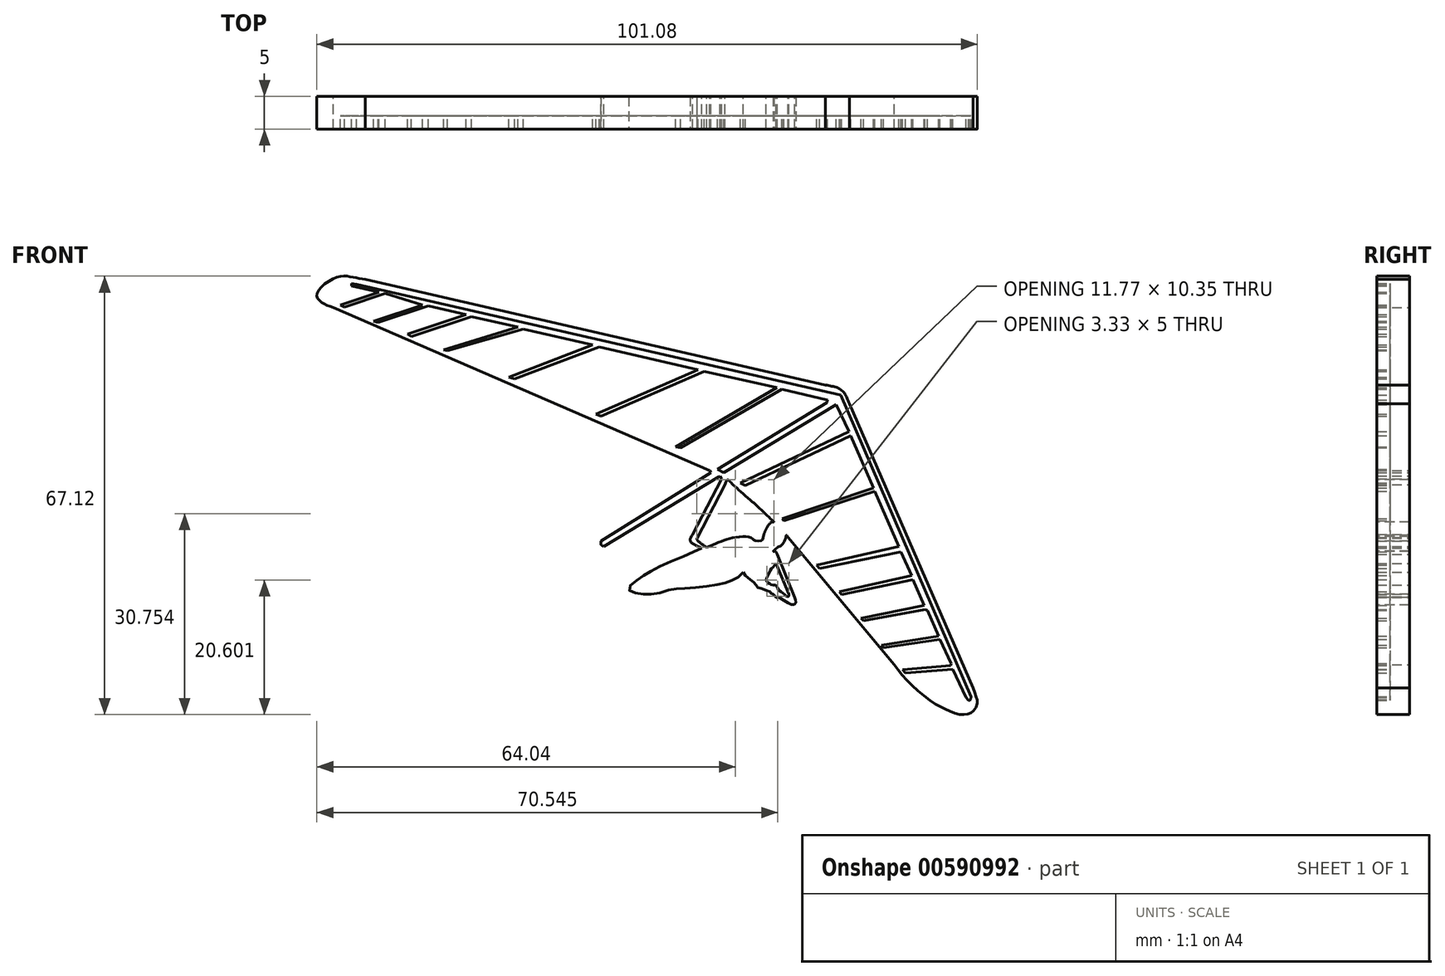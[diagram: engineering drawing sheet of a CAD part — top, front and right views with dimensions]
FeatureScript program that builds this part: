
annotation { "Feature Type Name" : "Feature", "Feature Type Description" : "" }
export const myFeature = defineFeature(function(context is Context, id is Id, definition is map)
    precondition{}
    {
        {
            var Q0;
            Q0=qCreatedBy(makeId("Front.planeOp"),FACE);
            var sketch = newSketch(context, id + "F0", { "sketchPlane" : qUnion([Q0])});
            skFitSpline(sketch, "E0", {"points": [v(-69.22, 30.45) * mm, v(-71.12, 31.32) * mm, v(-71.66, 32.62) * mm, v(-68.68, 35.07) * mm, v(-66.35, 35.12) * mm, v(-64.29, 34.74) * mm], "startDerivative": vector(-10.93, 3.69) * mm, "endDerivative": vector(10.85, -2) * mm});
            skFitSpline(sketch, "E1", {"points": [v(6.12, 18.58) * mm, v(8, 18.14) * mm, v(9.02, 17.32) * mm, v(9.77, 15.73) * mm], "startDerivative": vector(5.63, -0.88) * mm, "endDerivative": vector(1.94, -5.07) * mm});
            skLineSegment(sketch, "E2", {"start": v(-64.29, 34.74) * mm, "end": v(6.12, 18.58) * mm});
            skLineSegment(sketch, "E3", {"start": v(9.77, 15.73) * mm, "end": v(28.73, -27.8) * mm});
            skFitSpline(sketch, "E4", {"points": [v(28.73, -27.8) * mm, v(29.23, -29.25) * mm, v(29.34, -30.21) * mm, v(28.73, -31.36) * mm, v(28, -31.75) * mm, v(26.66, -31.82) * mm, v(24.7, -31.13) * mm, v(22.51, -29.98) * mm, v(18.95, -26.99) * mm, v(16.65, -24.23) * mm], "startDerivative": vector(5.52, -15.59) * mm, "endDerivative": vector(-13.52, 17.82) * mm});
            skLineSegment(sketch, "E5", {"start": v(16.65, -24.23) * mm, "end": v(0.4, -4.7) * mm});
            skFitSpline(sketch, "E6", {"points": [v(0.4, -4.7) * mm, v(0.16, -4.41) * mm, v(0, -4.91) * mm, v(-0.32, -5.6) * mm, v(-0.74, -6.05) * mm, v(-1.2, -6.27) * mm, v(-1.74, -6.74) * mm, v(-1.86, -6.88) * mm, v(-1.59, -6.85) * mm, v(-1.25, -7.34) * mm], "startDerivative": vector(-2.75, 4.77) * mm, "endDerivative": vector(2.1, -5.53) * mm});
            skLineSegment(sketch, "E7", {"start": v(-1.25, -7.34) * mm, "end": v(1.41, -13.93) * mm});
            skFitSpline(sketch, "E8", {"points": [v(1.41, -13.93) * mm, v(1.57, -14.39) * mm, v(1.54, -14.85) * mm, v(1.18, -15.06) * mm, v(0.45, -14.76) * mm, v(-0.65, -14.13) * mm, v(-1.02, -13.93) * mm, v(-1.45, -13.93) * mm, v(-1.58, -13.74) * mm, v(-1.86, -13.45) * mm, v(-2.2, -13.35) * mm, v(-2.28, -13.1) * mm, v(-2.74, -12.95) * mm, v(-3.44, -12.62) * mm, v(-4.22, -12.4) * mm, v(-4.53, -11.97) * mm, v(-5.4, -11.16) * mm, v(-5.93, -10.76) * mm, v(-6.45, -10.1) * mm], "startDerivative": vector(3.77, -9) * mm, "endDerivative": vector(-7.55, 10.71) * mm});
            skFitSpline(sketch, "E9", {"points": [v(-6.45, -10.1) * mm, v(-7.4, -10.92) * mm, v(-8.68, -11.52) * mm, v(-10.03, -11.9) * mm, v(-12.7, -12.3) * mm, v(-15.75, -12.57) * mm, v(-17.28, -12.67) * mm, v(-19.34, -13.27) * mm, v(-21.21, -13.44) * mm, v(-22.7, -13.31) * mm, v(-23.86, -12.9) * mm, v(-23.86, -12.27) * mm, v(-22.68, -11.23) * mm, v(-21.15, -10.25) * mm, v(-18.92, -9.02) * mm, v(-15.02, -7.38) * mm, v(-12.8, -6.36) * mm], "startDerivative": vector(-17.26, -17.14) * mm, "endDerivative": vector(28.06, 13.44) * mm});
            skFitSpline(sketch, "E10", {"points": [v(-12.8, -6.36) * mm, v(-13.52, -6.07) * mm, v(-14.23, -5.64) * mm, v(-14.5, -5.4) * mm, v(-14.58, -5.03) * mm, v(-14.18, -4.26) * mm], "startDerivative": vector(-3.2, 1.1) * mm, "endDerivative": vector(2.29, 3.47) * mm});
            skLineSegment(sketch, "E11", {"start": v(-14.18, -4.26) * mm, "end": v(-9.77, 4.2) * mm});
            skLineSegment(sketch, "E12", {"start": v(-9.77, 4.2) * mm, "end": v(-10.04, 4.64) * mm});
            skLineSegment(sketch, "E13", {"start": v(-10.04, 4.64) * mm, "end": v(-10.22, 4.53) * mm});
            skLineSegment(sketch, "E14", {"start": v(-10.22, 4.53) * mm, "end": v(-27.8, -6.12) * mm});
            skFitSpline(sketch, "E15", {"points": [v(-27.8, -6.12) * mm, v(-28.21, -5.86) * mm, v(-28.24, -5.33) * mm], "startDerivative": vector(-1.02, 0.4) * mm, "endDerivative": vector(0.13, 1.17) * mm});
            skLineSegment(sketch, "E16", {"start": v(-28.24, -5.33) * mm, "end": v(-11.39, 5.16) * mm});
            skLineSegment(sketch, "E17", {"start": v(-11.39, 5.16) * mm, "end": v(-11.6, 5.5) * mm});
            skLineSegment(sketch, "E18", {"start": v(-11.6, 5.5) * mm, "end": v(-69.22, 30.45) * mm});
            skLineSegment(sketch, "E19", {"start": v(-1.44, -8.76) * mm, "end": v(0.5, -13.44) * mm});
            skFitSpline(sketch, "E20", {"points": [v(0.5, -13.44) * mm, v(0.5, -13.76) * mm, v(0.29, -13.82) * mm, v(-0.17, -13.44) * mm, v(-0.75, -13.04) * mm, v(-1.19, -12.56) * mm, v(-1.44, -12.1) * mm, v(-2.05, -12.04) * mm, v(-2.4, -11.85) * mm, v(-2.93, -11.39) * mm, v(-2.74, -10.73) * mm, v(-2.26, -9.74) * mm, v(-1.86, -9.26) * mm, v(-1.44, -8.76) * mm], "startDerivative": vector(1.22, -6.57) * mm, "endDerivative": vector(5.17, 6.38) * mm});
            skLineSegment(sketch, "E21", {"start": v(-9.24, 3.35) * mm, "end": v(-13.53, -4.86) * mm});
            skFitSpline(sketch, "E22", {"points": [v(-13.53, -4.86) * mm, v(-13.53, -5.1) * mm, v(-12.04, -6.28) * mm], "startDerivative": vector(-0.26, -0.8) * mm, "endDerivative": vector(2.75, -1.86) * mm});
            skFitSpline(sketch, "E23", {"points": [v(-12.04, -6.28) * mm, v(-10.67, -5.69) * mm, v(-9.44, -5.2) * mm, v(-8.32, -4.86) * mm, v(-6.72, -4.63) * mm, v(-5.48, -4.72) * mm, v(-4.96, -5.04) * mm, v(-4.69, -5.22) * mm, v(-3.64, -5.22) * mm, v(-3.38, -4.58) * mm, v(-2.62, -2.88) * mm, v(-2.02, -2.37) * mm, v(-1.77, -2.35) * mm, v(-2.35, -1.82) * mm, v(-3.73, -0.48) * mm, v(-8.19, 3.5) * mm, v(-8.73, 4.04) * mm, v(-8.93, 4.05) * mm, v(-9.24, 3.35) * mm], "startDerivative": vector(23.43, 10.24) * mm, "endDerivative": vector(-6.86, -22.07) * mm});
            skLineSegment(sketch, "E24", {"start": v(-2.77, -3.12) * mm, "end": v(-3.96, -0.27) * mm});
            skLineSegment(sketch, "E25", {"start": v(-5.04, 0.7) * mm, "end": v(-3.28, -4.24) * mm});
            skLineSegment(sketch, "E26", {"start": v(-65.62, 34.03) * mm, "end": v(7.55, 17.23) * mm});
            skLineSegment(sketch, "E27", {"start": v(7.55, 17.23) * mm, "end": v(8.47, 17.02) * mm});
            skLineSegment(sketch, "E28", {"start": v(8.47, 17.02) * mm, "end": v(28.38, -29.11) * mm});
            skLineSegment(sketch, "E29", {"start": v(28.38, -29.11) * mm, "end": v(28.32, -29.59) * mm});
            skLineSegment(sketch, "E30", {"start": v(28.32, -29.59) * mm, "end": v(28.24, -29.72) * mm});
            skLineSegment(sketch, "E31", {"start": v(28.24, -29.72) * mm, "end": v(28.02, -29.67) * mm});
            skLineSegment(sketch, "E32", {"start": v(28.02, -29.67) * mm, "end": v(27.64, -29.26) * mm});
            skLineSegment(sketch, "E33", {"start": v(27.64, -29.26) * mm, "end": v(25.6, -24.93) * mm});
            skLineSegment(sketch, "E34", {"start": v(25.6, -24.93) * mm, "end": v(18.37, -25.52) * mm});
            skLineSegment(sketch, "E35", {"start": v(18.37, -25.52) * mm, "end": v(17.92, -25.02) * mm});
            skLineSegment(sketch, "E36", {"start": v(17.92, -25.02) * mm, "end": v(25.32, -24.35) * mm});
            skLineSegment(sketch, "E37", {"start": v(25.32, -24.35) * mm, "end": v(25.37, -24.05) * mm});
            skLineSegment(sketch, "E38", {"start": v(25.37, -24.05) * mm, "end": v(23.62, -20.36) * mm});
            skLineSegment(sketch, "E39", {"start": v(23.62, -20.36) * mm, "end": v(15.03, -21.65) * mm});
            skLineSegment(sketch, "E40", {"start": v(15.03, -21.65) * mm, "end": v(14.68, -21.24) * mm});
            skLineSegment(sketch, "E41", {"start": v(14.68, -21.24) * mm, "end": v(23.44, -19.82) * mm});
            skLineSegment(sketch, "E42", {"start": v(23.44, -19.82) * mm, "end": v(21.73, -15.89) * mm});
            skLineSegment(sketch, "E43", {"start": v(21.73, -15.89) * mm, "end": v(21.38, -15.8) * mm});
            skLineSegment(sketch, "E44", {"start": v(21.38, -15.8) * mm, "end": v(11.93, -17.53) * mm});
            skLineSegment(sketch, "E45", {"start": v(11.93, -17.53) * mm, "end": v(11.59, -17.12) * mm});
            skLineSegment(sketch, "E46", {"start": v(11.59, -17.12) * mm, "end": v(21.23, -15.13) * mm});
            skLineSegment(sketch, "E47", {"start": v(21.23, -15.13) * mm, "end": v(19.54, -11.2) * mm});
            skLineSegment(sketch, "E48", {"start": v(19.54, -11.2) * mm, "end": v(8.57, -13.48) * mm});
            skLineSegment(sketch, "E49", {"start": v(8.57, -13.48) * mm, "end": v(8.24, -13.09) * mm});
            skLineSegment(sketch, "E50", {"start": v(8.24, -13.09) * mm, "end": v(19.35, -10.55) * mm});
            skLineSegment(sketch, "E51", {"start": v(19.35, -10.55) * mm, "end": v(17.65, -6.99) * mm});
            skLineSegment(sketch, "E52", {"start": v(17.65, -6.99) * mm, "end": v(5.2, -9.5) * mm});
            skLineSegment(sketch, "E53", {"start": v(5.2, -9.5) * mm, "end": v(4.8, -9.01) * mm});
            skLineSegment(sketch, "E54", {"start": v(4.8, -9.01) * mm, "end": v(17.36, -6.15) * mm});
            skLineSegment(sketch, "E55", {"start": v(17.36, -6.15) * mm, "end": v(13.67, 2.32) * mm});
            skLineSegment(sketch, "E56", {"start": v(13.67, 2.32) * mm, "end": v(-0.24, -2.18) * mm});
            skLineSegment(sketch, "E57", {"start": v(-0.24, -2.18) * mm, "end": v(-0.5, -1.87) * mm});
            skLineSegment(sketch, "E58", {"start": v(-0.5, -1.87) * mm, "end": v(13.49, 2.83) * mm});
            skLineSegment(sketch, "E59", {"start": v(13.49, 2.83) * mm, "end": v(10, 10.84) * mm});
            skLineSegment(sketch, "E60", {"start": v(10, 10.84) * mm, "end": v(-6.14, 3.17) * mm});
            skLineSegment(sketch, "E61", {"start": v(-6.14, 3.17) * mm, "end": v(-6.9, 3.56) * mm});
            skLineSegment(sketch, "E62", {"start": v(-6.9, 3.56) * mm, "end": v(9.72, 11.47) * mm});
            skLineSegment(sketch, "E63", {"start": v(9.72, 11.47) * mm, "end": v(7.77, 15.57) * mm});
            skLineSegment(sketch, "E64", {"start": v(7.77, 15.57) * mm, "end": v(-6.9, 6.69) * mm});
            skLineSegment(sketch, "E65", {"start": v(-6.9, 6.69) * mm, "end": v(-9.42, 5.17) * mm});
            skLineSegment(sketch, "E66", {"start": v(-9.42, 5.17) * mm, "end": v(-10.42, 5.69) * mm});
            skLineSegment(sketch, "E67", {"start": v(-10.42, 5.69) * mm, "end": v(6.4, 15.87) * mm});
            skLineSegment(sketch, "E68", {"start": v(6.4, 15.87) * mm, "end": v(6.42, 16.3) * mm});
            skLineSegment(sketch, "E69", {"start": v(6.42, 16.3) * mm, "end": v(5.83, 16.44) * mm});
            skLineSegment(sketch, "E70", {"start": v(5.83, 16.44) * mm, "end": v(-0.56, 17.9) * mm});
            skLineSegment(sketch, "E71", {"start": v(-0.56, 17.9) * mm, "end": v(-16.07, 8.95) * mm});
            skLineSegment(sketch, "E72", {"start": v(-16.07, 8.95) * mm, "end": v(-16.83, 9.12) * mm});
            skLineSegment(sketch, "E73", {"start": v(-16.83, 9.12) * mm, "end": v(-1.34, 18.16) * mm});
            skLineSegment(sketch, "E74", {"start": v(-1.34, 18.16) * mm, "end": v(-12.4, 20.7) * mm});
            skLineSegment(sketch, "E75", {"start": v(-12.4, 20.7) * mm, "end": v(-28.2, 13.8) * mm});
            skLineSegment(sketch, "E76", {"start": v(-28.2, 13.8) * mm, "end": v(-29, 14.14) * mm});
            skLineSegment(sketch, "E77", {"start": v(-29, 14.14) * mm, "end": v(-13.35, 20.95) * mm});
            skLineSegment(sketch, "E78", {"start": v(-13.35, 20.95) * mm, "end": v(-28.48, 24.42) * mm});
            skLineSegment(sketch, "E79", {"start": v(-28.48, 24.42) * mm, "end": v(-41.44, 19.55) * mm});
            skLineSegment(sketch, "E80", {"start": v(-41.44, 19.55) * mm, "end": v(-42.32, 19.75) * mm});
            skLineSegment(sketch, "E81", {"start": v(-42.32, 19.75) * mm, "end": v(-29.47, 24.71) * mm});
            skLineSegment(sketch, "E82", {"start": v(-29.47, 24.71) * mm, "end": v(-40.1, 27.15) * mm});
            skLineSegment(sketch, "E83", {"start": v(-40.1, 27.15) * mm, "end": v(-51.7, 23.83) * mm});
            skLineSegment(sketch, "E84", {"start": v(-51.7, 23.83) * mm, "end": v(-52.31, 23.97) * mm});
            skLineSegment(sketch, "E85", {"start": v(-52.31, 23.97) * mm, "end": v(-40.94, 27.44) * mm});
            skLineSegment(sketch, "E86", {"start": v(-40.94, 27.44) * mm, "end": v(-48.04, 29.07) * mm});
            skLineSegment(sketch, "E87", {"start": v(-48.04, 29.07) * mm, "end": v(-57.23, 25.97) * mm});
            skLineSegment(sketch, "E88", {"start": v(-57.23, 25.97) * mm, "end": v(-57.84, 26.38) * mm});
            skLineSegment(sketch, "E89", {"start": v(-57.84, 26.38) * mm, "end": v(-48.9, 29.39) * mm});
            skLineSegment(sketch, "E90", {"start": v(-48.9, 29.39) * mm, "end": v(-54.67, 30.72) * mm});
            skLineSegment(sketch, "E91", {"start": v(-54.67, 30.72) * mm, "end": v(-62.31, 28.15) * mm});
            skLineSegment(sketch, "E92", {"start": v(-62.31, 28.15) * mm, "end": v(-63.06, 28.32) * mm});
            skLineSegment(sketch, "E93", {"start": v(-63.06, 28.32) * mm, "end": v(-55.53, 30.85) * mm});
            skLineSegment(sketch, "E94", {"start": v(-55.53, 30.85) * mm, "end": v(-61.25, 32.62) * mm});
            skLineSegment(sketch, "E95", {"start": v(-61.25, 32.62) * mm, "end": v(-67.45, 30.53) * mm});
            skLineSegment(sketch, "E96", {"start": v(-67.45, 30.53) * mm, "end": v(-68.12, 30.82) * mm});
            skLineSegment(sketch, "E97", {"start": v(-68.12, 30.82) * mm, "end": v(-62.22, 32.81) * mm});
            skLineSegment(sketch, "E98", {"start": v(-62.22, 32.81) * mm, "end": v(-63.04, 33) * mm});
            skLineSegment(sketch, "E99", {"start": v(-63.04, 33) * mm, "end": v(-66.4, 33.77) * mm});
            skLineSegment(sketch, "E100", {"start": v(-66.4, 33.77) * mm, "end": v(-66.4, 34.11) * mm});
            skLineSegment(sketch, "E101", {"start": v(-66.4, 34.11) * mm, "end": v(-65.62, 34.03) * mm});
            skSolve(sketch);
        }
        {
            var Q0;
            Q0=makeQuery(id+"F0.imprint","IMPRINT",FACE,{"disambiguationData":[TD([[makeQuery(id+"F0.imprint","IMPRINT",EDGE,{"derivedFrom":sQuery(id+"F0.wireOp",EDGE,"E26")}),-1.0]])]});
            extrude(context, id + "F1", {"entities" : qUnion([Q0]), "depth" : 3 * mm, "offsetDistance" : 25 * mm});
        }
        {
            var Q0;
            Q0=makeQuery(id+"F0.imprint","IMPRINT",FACE,{"disambiguationData":[TD([[makeQuery(id+"F0.imprint","IMPRINT",EDGE,{"derivedFrom":sQuery(id+"F0.wireOp",EDGE,"E0")}),-1.0]])]});
            extrude(context, id + "F2", {"entities" : qUnion([Q0]), "operationType" : NewBodyOperationType.ADD, "depth" : 5 * mm, "offsetDistance" : 25 * mm});
        }
    });
